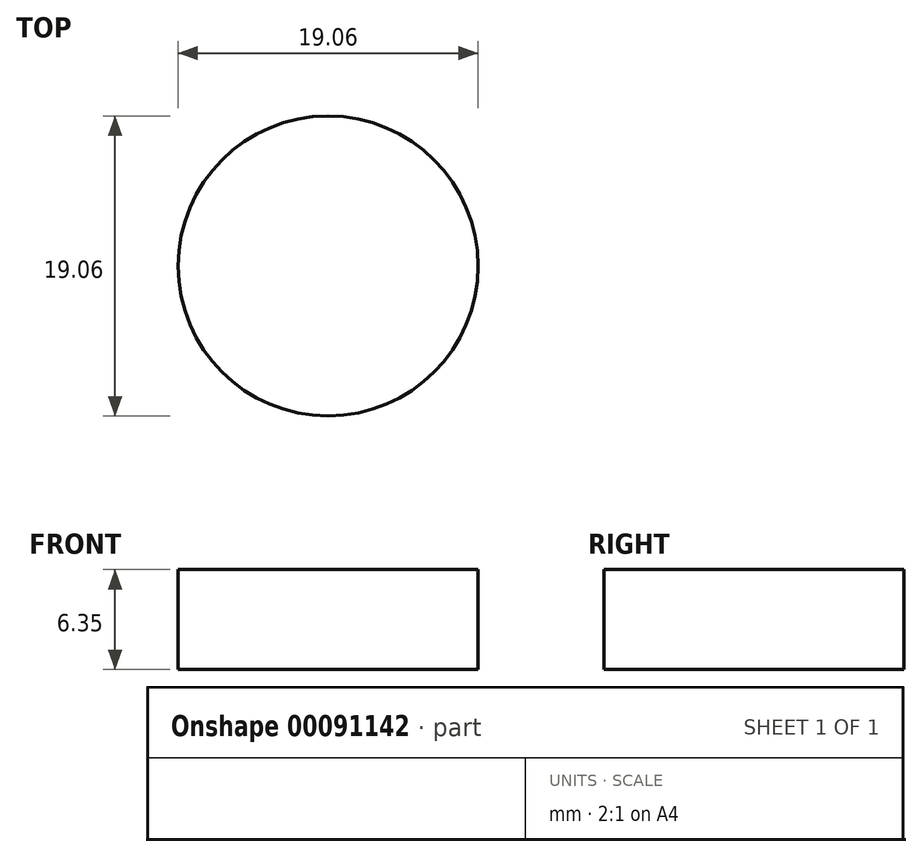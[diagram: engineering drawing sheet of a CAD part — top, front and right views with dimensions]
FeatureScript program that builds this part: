
annotation { "Feature Type Name" : "Feature", "Feature Type Description" : "" }
export const myFeature = defineFeature(function(context is Context, id is Id, definition is map)
    precondition{}
    {
        {
            var Q0;
            Q0=qCreatedBy(makeId("Top.planeOp"),FACE);
            var sketch = newSketch(context, id + "F0", { "sketchPlane" : qUnion([Q0])});
            skCircle(sketch, "E0", {"center": v(0, 0) * mm, "radius": 9.53 * mm});
            skSolve(sketch);
        }
        {
            var Q0;
            Q0=qSketchRegion(id+"F0",true);
            extrude(context, id + "F1", {"entities" : qUnion([Q0]), "offsetDistance" : 25 * mm, "depth" : 6.35 * mm});
        }
    });
